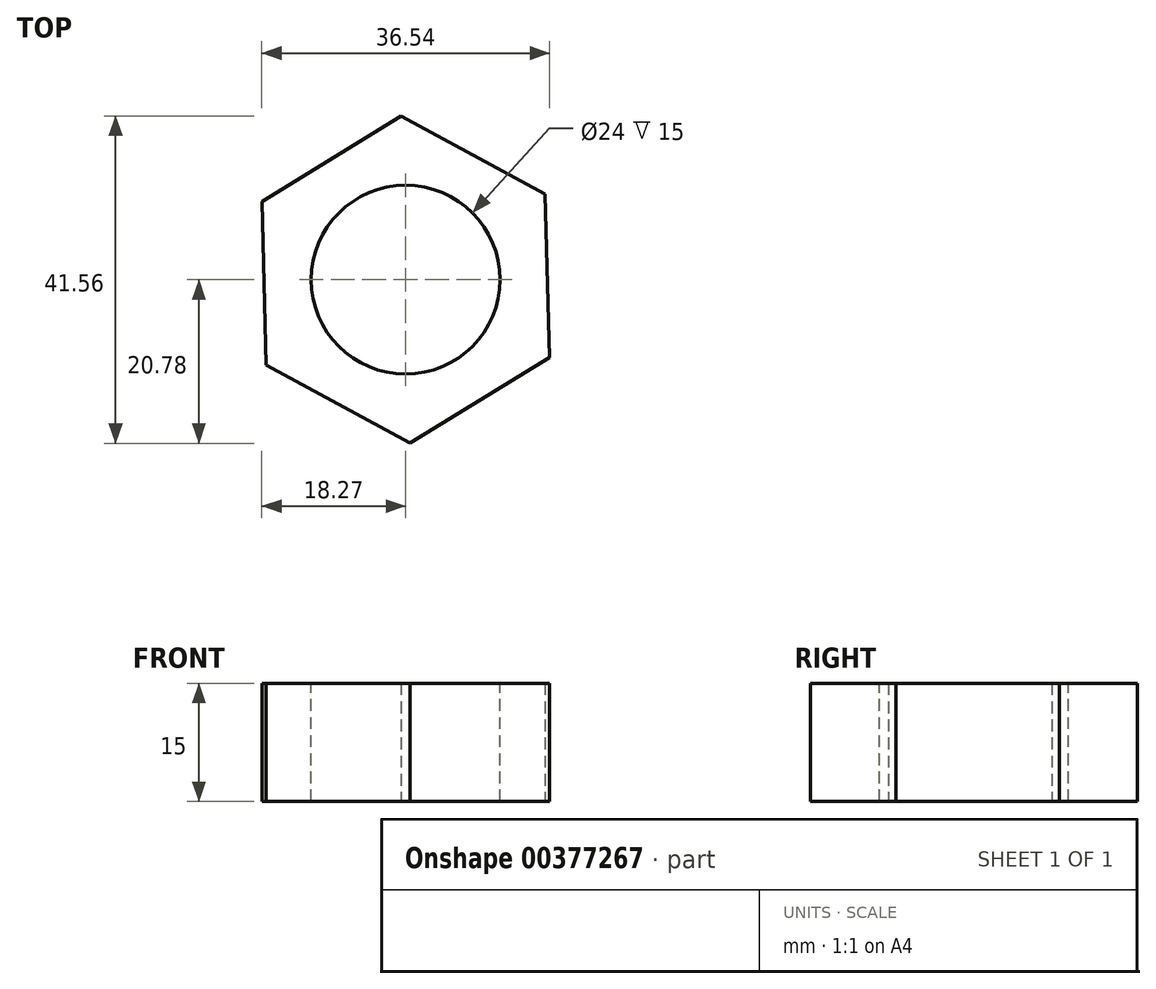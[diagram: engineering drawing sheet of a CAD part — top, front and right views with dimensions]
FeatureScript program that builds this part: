
annotation { "Feature Type Name" : "Feature", "Feature Type Description" : "" }
export const myFeature = defineFeature(function(context is Context, id is Id, definition is map)
    precondition{}
    {
        {
            var Q0;
            Q0=qCreatedBy(makeId("Top.planeOp"),FACE);
            var sketch = newSketch(context, id + "F0", { "sketchPlane" : qUnion([Q0])});
            skCircle(sketch, "E0.cCircle", {"center": v(0, 0) * mm, "radius": 18 * mm, "construction": true});
            skLineSegment(sketch, "E0.0", {"start": v(-18.27, 9.91) * mm, "end": v(-0.55, 20.78) * mm});
            skLineSegment(sketch, "E0.1", {"start": v(-0.55, 20.78) * mm, "end": v(17.72, 10.87) * mm});
            skLineSegment(sketch, "E0.2", {"start": v(17.72, 10.87) * mm, "end": v(18.27, -9.91) * mm});
            skLineSegment(sketch, "E0.3", {"start": v(18.27, -9.91) * mm, "end": v(0.55, -20.78) * mm});
            skLineSegment(sketch, "E0.4", {"start": v(0.55, -20.78) * mm, "end": v(-17.72, -10.87) * mm});
            skLineSegment(sketch, "E0.5", {"start": v(-17.72, -10.87) * mm, "end": v(-18.27, 9.91) * mm});
            skPoint(sketch, "E0.0.midPoint", {"position": v(-9.4, 15.34) * mm});
            skSolve(sketch);
        }
        {
            var Q0;
            Q0=makeQuery(id+"F0.imprint","IMPRINT",FACE,{"disambiguationData":[TD([[makeQuery(id+"F0.imprint","IMPRINT",EDGE,{"derivedFrom":sQuery(id+"F0.wireOp",EDGE,"E0.0")}),-1.0]])]});
            extrude(context, id + "F1", {"entities" : qUnion([Q0]), "depth" : 15 * mm});
        }
        {
            var Q0;
            Q0=makeQuery(id+"F1.opExtrude","CAP_FACE",FACE,{"disambiguationData":[OSD([sQuery(id+"F0.wireOp",EDGE,"E0.0"),sQuery(id+"F0.wireOp",EDGE,"E0.1"),sQuery(id+"F0.wireOp",EDGE,"E0.2"),sQuery(id+"F0.wireOp",EDGE,"E0.3"),sQuery(id+"F0.wireOp",EDGE,"E0.4"),sQuery(id+"F0.wireOp",EDGE,"E0.5")])],"isStart":false});
            var sketch = newSketch(context, id + "F2", { "sketchPlane" : qUnion([Q0])});
            skPoint(sketch, "E1", {"position": v(0, 0) * mm});
            skSolve(sketch);
        }
        {
            var Q0;
            Q0=sQuery(id+"F2.wireOp",VERTEX,"E1");
            var Q1;
            Q1=makeQuery(id+"F1.opExtrude","SWEPT_BODY",BODY,{"disambiguationData":[OSD([sQuery(id+"F0.wireOp",EDGE,"E0.0"),sQuery(id+"F0.wireOp",EDGE,"E0.1"),sQuery(id+"F0.wireOp",EDGE,"E0.2"),sQuery(id+"F0.wireOp",EDGE,"E0.3"),sQuery(id+"F0.wireOp",EDGE,"E0.4"),sQuery(id+"F0.wireOp",EDGE,"E0.5")])]});
            hole(context, id + "F3", {"style" : HoleStyle.SIMPLE, "endStyle" : HoleEndStyle.THROUGH, "standardTappedOrClearance" : lookupTablePath({ "standard" : "ISO", "size" : "24", "type" : "Drilled" }), "standardBlindInLast" : lookupTablePath({ "standard" : "ISO", "size" : "24", "type" : "Drilled" }), "holeDiameter" : 24 * mm, "isTappedThrough" : true, "tappedDepth" : 12 * mm, "tapClearance" : 3, "locations" : qUnion([Q0]), "scope" : qUnion([Q1])});
        }
    });
